# Revit family: BE_88978_de_DE
name_source: partatom
category: Leuchten
units: mm (PartAtom-declared; Revit-internal decimal feet)

## family parameters
Basisbauteil = Fläche
Beim Laden mit Abzugskörper schneiden = Ja
Bemaßung runder Anschluss = Durchmesser verwenden
Gemeinsam genutzt = Nein
Lichtquelle = Nein
Raumberechnungspunkt = Ja
Teiletyp = Normal

## types (4) — shared parameters
AC/DC = AC/DC
Aktualisierung = 2024-03-08T04:00:03
Anschlussleitung = 4.0 m X05BQ-F 5 G 1 mm²
BEGA_IES = Ja
BEGA_IES3 = Ja
BEGA_Intern = Ja
BEGA_Intern_Konstruktion = Ja
BEGA_Intern_an = Ja
BEGA_Intern_aus = Ja
Befestigungsabstand = 240 x 240 mm
Befestigungsbohrung = Ø 18 mm
Beschreibung = Lichtbauelement
Beschreibung_Sonderanfertigung = Hier können Sie Informationen zur Sonderanfertigung eintragen.
CE_Konformität = ja
ENEC = ja
Energieeffizienzklasse = LED A++ - A
Farbwiedergabeindex = CRI > 80
Frequenz = 0/50-60 Hz
Gewicht = 50.0 kg
Hersteller = BEGA
Lampe = LED 37.6 W
Lastklassifizierung = Beleuchtung
Lebensdauerkriterien = L80B50 @ ta 25 °C = 200000 h
Logo = <Keine Auswahl>
M_W = Nein
Material_02 = BEGA_Oberfläche_Silber_matt
Material_06 = BEGA_Oberfläche_Edelstahl_gebürstet
Material_08 = BEGA_Oberfläche_Stahl_verzinkt
Material_09 = BEGA_Glas_klar
Material_15 = BEGA_Leuchtmedium_matt
Material_17 = BEGA_Reflektor
Material_18 = BEGA_Gummi_schwarz
Produktdatenblatt = https://cdn.bega.com
Scheinlast = 0 VA
Schutzart = IP 65
Schutzklasse = I
Sonderanfertigung = Nein
Spannung = 240 V
URL = https://www.bega.com
Umgebungstemperatur = 25 °C
Windangriffsfläche = 0.9 m²
zero-valued in all types: BEGA_IES_Y1, BEGA_IES_Y2, Vorgabe-Ansicht

## per-type parameters (varying)
| type | BEGA_IES1 | BEGA_IES2 | Bestellnummer | Farbtemperatur | LED_Modulbezeichnung | Lampenlichtstrom | Leuchtenlichtstrom | M_A | M_G | Modell |
| BEGA_88978_Grafit_K4 | Nein | Ja | 88978K4 | 4000 K | 8x LED-0147/840 | 8080 lm | 5388 lm | Nein | Ja | 88978K4 |
| BEGA_88978_Grafit_K3 | Ja | Nein | 88978K3 | 3000 K | 8x LED-0147/830 | 7840 lm | 5228 lm | Nein | Ja | 88978K3 |
| BEGA_88978_Silber_K3 | Ja | Nein | 88978AK3 | 3000 K | 8x LED-0147/830 | 7840 lm | 5228 lm | Ja | Nein | 88978AK3 |
| BEGA_88978_Silber_K4 | Nein | Ja | 88978AK4 | 4000 K | 8x LED-0147/840 | 8080 lm | 5388 lm | Ja | Nein | 88978AK4 |

## geometry (parser evidence)
native form markers: Sweep x28
no freeform markers — native parametric forms only
